# Revit family: Tub_Shower_Trim-DXV-Percy-D351056X0_Series
name_source: partatom
category: Plumbing Fixtures
revit_build: Autodesk Revit 2014 (Build: 20130308_1515(x64)
units: mm (PartAtom-declared; Revit-internal decimal feet)

## types (6) — shared parameters
Assembly Code = D2010710
CW Connection = Yes
CWFU = 3
Cold Water Connection Diameter = 1/2"
Cold Water Connection Height = 48"
Cold Water Connection Radius = 1/4"
Cold Water Connection Width = 2 3/4"
Default Elevation = 44"
Description = Percy® Pressure Balance Tub/Shower Valve Trim With Diverter
HW Connection = Yes
HWFU = 3
Height = 7 5/16"
Hot Water Connection Diameter = 1"
Hot Water Connection Height = 48"
Hot Water Connection Radius = 1/4"
Hot Water Connection Width = 2 3/4"
Installation Type = Wall Mounted
Length = 3"
Manufacturer = DXV
Plug Visiblilty = No
Price = Prices may vary. Please consult Manufacturer Representative for most up-to-date price list.
Product Page URL = https://www.dxv.com
Spout Connection = 1/4"
Spout Connection Description = 1/2'' NPT Spout Supply Outlet
Tempered Water Connection = Yes
Tempered Water Connection Diameter = 1/2"
Tempered Water Connection Radius = 1/4"
URL = www.dxv.com
Vent Connection = No
WFU = 4
Warranty Documentation Link = https://www.dxv.com
Waste Connection = No
Width = 7 5/16"

## per-type parameters (varying)
| type | ADA Compliant | Cross Handle Option | Finish | Lever Handle Option | Material | Tri-Spoke Handle Option |
| D35105600.100 | Yes | No | Metal-DXV-100-Polished Chrome | Yes | Metal-DXV-100-Polished Chrome | No |
| D35105600.144 | Yes | No | Metal-DXV-144-Brushed Nickel | Yes | Metal-DXV-144-Brushed Nickel | No |
| D35105640.100 | No | Yes | Metal-DXV-100-Polished Chrome | No | Metal-DXV-100-Polished Chrome | No |
| D35105640.144 | No | Yes | Metal-DXV-144-Brushed Nickel | No | Metal-DXV-144-Brushed Nickel | No |
| D35105670.100 | Yes | No | Metal-DXV-100-Polished Chrome | No | Metal-DXV-100-Polished Chrome | Yes |
| D35105670.144 | Yes | No | Metal-DXV-144-Brushed Nickel | No | Metal-DXV-144-Brushed Nickel | Yes |

note: column(s) folded — value = type name in every type: Model

## geometry (parser evidence)
native form markers: Sweep x1
no freeform markers — native parametric forms only
